FCSTD DOCUMENT  (FreeCAD 0.21R33771 (Git))
Label: enclousre
License: All rights reserved
LicenseURL: http://en.wikipedia.org/wiki/All_rights_reserved
objects: Part::Feature×48, App::Link×17, App::Part×7, Sketcher::SketchObject×3, PartDesign::Body×2, PartDesign::CoordinateSystem×1, Spreadsheet::Sheet×1, PartDesign::Pad×1
note: 56 computed .brp shape members not serialized (recipe doc carries the construction recipe); baked Part::Feature solids carry a one-line shape summary decoded from their .brp

FEATURE [PartDesign::CoordinateSystem] Local_CS_4743
  AttacherType = Attacher::AttachEngine3D
  MapMode = 2
  Support = -> [X_Axis001]
FEATURE [Part::Feature] Pcb_4743
  Placement = pos=(-69.596,105.156,0) rot=(0,0,1;0rad)
  shape: bbox 160.8 x 51.31 x 1.6 mm, 62 faces (baked)
FEATURE [Sketcher::SketchObject] PCB_Sketch_4743
  FullyConstrained = false
  sketch-geometry (4):
    g0: LineSegment StartX=0 StartY=51.308 StartZ=0 EndX=160.782 EndY=51.308 EndZ=0
    g1: LineSegment StartX=160.782 StartY=51.308 StartZ=0 EndX=160.782 EndY=0 EndZ=0
    g2: LineSegment StartX=160.782 StartY=0 StartZ=0 EndX=0 EndY=0 EndZ=0
    g3: LineSegment StartX=0 StartY=0 StartZ=0 EndX=0 EndY=51.308 EndZ=0
  constraints (4):
    c: Coincident(g2,g3)
    c: Coincident(g0,g3)
    c: Coincident(g1,g2)
    c: Coincident(g0,g1)
FEATURE [Part::Feature] Shape  label="R8_R_0805_2012Metric_542de8cd5894"
  Placement = pos=(126.088,23.921,0) rot=(0,0,1;3.14159rad)
  shape: bbox 2 x 1.2 x 0.45 mm, 26 faces (baked)
FEATURE [Part::Feature] Shape001  label="D4_LED_0805_2012Metric_c15a0e7d9ebd"
  Placement = pos=(60.614,23.921,0) rot=(0,0,1;0rad)
  shape: bbox 2 x 1.25 x 1.1 mm, 50 faces (baked)
FEATURE [App::Link] D4_LED_0805_2012Metric_c15a0e7d9ebd_ln_  label="D8_LED_0805_2012Metric_47b09096554b"
  LinkPlacement = pos=(121.678,23.921,0) rot=(0,0,1;0rad)
  LinkedObject = -> Shape001
  Placement = pos=(121.678,23.921,0) rot=(0,0,1;0rad)
FEATURE [Part::Feature] Arduino_Nano_WithMountingHoles
  shape: bbox 43.59 x 4.635 x 18 mm, 378 faces, 0 solids (baked)
FEATURE [Part::Feature] Arduino_Nano_WithMountingHoles001
  Placement = pos=(-1.143,1.6,-7.62) rot=(0,0,1;0rad)
  shape: bbox 5 x 11.75 x 2.54 mm, 46 faces, 0 solids (baked)
FEATURE [Part::Feature] Arduino_Nano_WithMountingHoles002
  Placement = pos=(-1.143,1.6,-5.08) rot=(0,0,1;0rad)
  shape: bbox 5 x 11.75 x 2.54 mm, 46 faces, 0 solids (baked)
FEATURE [Part::Feature] Arduino_Nano_WithMountingHoles003
  Placement = pos=(-1.143,1.6,-10.16) rot=(0,0,1;0rad)
  shape: bbox 5 x 11.75 x 2.54 mm, 46 faces, 0 solids (baked)
FEATURE [Part::Feature] Arduino_Nano_WithMountingHoles004
  Placement = pos=(0,0,0) rot=(0.707107,0,0.707107;3.14159rad)
  shape: bbox 38.1 x 11.75 x 2.54 mm, 364 faces, 0 solids (baked)
FEATURE [Part::Feature] Arduino_Nano_WithMountingHoles005
  Placement = pos=(0,0,-15.24) rot=(0.707107,0,0.707107;3.14159rad)
  shape: bbox 38.1 x 11.75 x 2.54 mm, 364 faces, 0 solids (baked)
FEATURE [Part::Feature] Arduino_Nano_WithMountingHoles006
  Placement = pos=(23.85,1.75,-7.62) rot=(0,1,0;3.92699rad)
  shape: bbox 11.38 x 1.1 x 11.38 mm, 1867 faces, 0 solids (baked)
FEATURE [Part::Feature] Arduino_Nano_WithMountingHoles007
  Placement = pos=(29.05,0,-7.67) rot=(0.707107,0,-0.707107;3.14159rad)
  shape: bbox 10.32 x 1.9 x 9.71 mm, 717 faces, 0 solids (baked)
FEATURE [Part::Feature] Arduino_Nano_WithMountingHoles008
  Placement = pos=(21.86,0,-5.8) rot=(0.707107,0,-0.707107;3.14159rad)
  shape: bbox 3.8 x 0.6 x 1.7 mm, 74 faces, 0 solids (baked)
FEATURE [Part::Feature] Arduino_Nano_WithMountingHoles009
  Placement = pos=(21.86,0,-9) rot=(0.707107,0,-0.707107;3.14159rad)
  shape: bbox 3.8 x 0.6 x 1.7 mm, 74 faces, 0 solids (baked)
FEATURE [Part::Feature] Arduino_Nano_WithMountingHoles010
  Placement = pos=(36.75,0,-7.6) rot=(0.707107,0,-0.707107;3.14159rad)
  shape: bbox 3.8 x 0.6 x 1.7 mm, 74 faces, 0 solids (baked)
FEATURE [Part::Feature] Arduino_Nano_WithMountingHoles011
  Placement = pos=(36.75,0,-12) rot=(0.707107,0,-0.707107;3.14159rad)
  shape: bbox 3.8 x 0.6 x 1.7 mm, 74 faces, 0 solids (baked)
FEATURE [Part::Feature] Arduino_Nano_WithMountingHoles012
  Placement = pos=(8.2,0,-2.6) rot=(0.707107,0,-0.707107;3.14159rad)
  shape: bbox 3.8 x 0.6 x 1.7 mm, 74 faces, 0 solids (baked)
FEATURE [Part::Feature] Arduino_Nano_WithMountingHoles013
  Placement = pos=(10.4,1.6,-2.8) rot=(0,0,1;0rad)
  shape: bbox 5.518 x 1.649 x 1.609 mm, 57 faces, 0 solids (baked)
FEATURE [Part::Feature] Arduino_Nano_WithMountingHoles014
  Placement = pos=(10.4,1.6,-5.55) rot=(0,0,1;0rad)
  shape: bbox 5.518 x 1.649 x 1.609 mm, 57 faces, 0 solids (baked)
FEATURE [Part::Feature] Arduino_Nano_WithMountingHoles015
  Placement = pos=(10.4,1.6,-12.5) rot=(0,0,1;0rad)
  shape: bbox 5.518 x 1.649 x 1.609 mm, 57 faces, 0 solids (baked)
FEATURE [Part::Feature] Arduino_Nano_WithMountingHoles016
  Placement = pos=(10.4,1.6,-9.05) rot=(0,0,1;0rad)
  shape: bbox 5.518 x 1.649 x 1.609 mm, 57 faces, 0 solids (baked)
FEATURE [Part::Feature] Arduino_Nano_WithMountingHoles017
  Placement = pos=(18.5113,1.6,-3.55414) rot=(0,-1,0;0.785398rad)
  shape: bbox 3.818 x 0.8 x 3.818 mm, 71 faces, 0 solids (baked)
FEATURE [Part::Feature] Arduino_Nano_WithMountingHoles018
  Placement = pos=(38.98,1.65,-7.62) rot=(0,-1,0;1.5708rad)
  shape: bbox 9.474 x 3.821 x 11.03 mm, 243 faces, 0 solids (baked)
FEATURE [Part::Feature] Arduino_Nano_WithMountingHoles019
  Placement = pos=(32.28,1.65,-7.62) rot=(0,1,0;1.5708rad)
  shape: bbox 8.2 x 4.5 x 7.7 mm, 127 faces, 0 solids (baked)
FEATURE [Part::Feature] Arduino_Nano_WithMountingHoles020 .. Arduino_Nano_WithMountingHoles024  x5 (patterned run collapsed; names and placements below)
  shape: bbox 9.422 x 2.565 x 0.5 mm, 31 faces, 0 solids (baked)
  placements: 5 in arithmetic series — first pos=(33.28,1.65,-9.22) rot=(0,1,0;1.5708rad), step (0,0,0.8), last pos=(33.28,1.65,-6.02) rot=(0,1,0;1.5708rad)
FEATURE [Part::Feature] Arduino_Nano_WithMountingHoles025
  Placement = pos=(37.2,0,-3.3) rot=(0.707107,0,0.707107;3.14159rad)
  shape: bbox 4 x 1.81 x 1.7 mm, 124 faces, 0 solids (baked)
FEATURE [Part::Feature] Arduino_Nano_WithMountingHoles026
  Placement = pos=(7.9,0,-5.6) rot=(0.707107,0,-0.707107;3.14159rad)
  shape: bbox 4 x 1.81 x 1.7 mm, 124 faces, 0 solids (baked)
FEATURE [Part::Feature] Arduino_Nano_WithMountingHoles027
  Placement = pos=(15.25,1.6,-8.05) rot=(0,1,0;1.5708rad)
  shape: bbox 2.8 x 2.156 x 5.2 mm, 77 faces, 0 solids (baked)
FEATURE [Part::Feature] Arduino_Nano_WithMountingHoles028
  Placement = pos=(15.25,3.25,-8.05) rot=(0,0,1;0rad)
  shape: bbox 3.003 x 1.653 x 4.003 mm, 100 faces, 0 solids (baked)
FEATURE [Part::Feature] Arduino_Nano_WithMountingHoles029
  Placement = pos=(6.1,0,-10.16) rot=(0.707107,0,-0.707107;3.14159rad)
  shape: bbox 8.3 x 1.69 x 6.5 mm, 198 faces, 0 solids (baked)
FEATURE [Part::Feature] Arduino_Nano_WithMountingHoles030
  Placement = pos=(11.43,0,-4.2) rot=(0.707107,0,0.707107;3.14159rad)
  shape: bbox 1.7 x 1.384 x 4.916 mm, 85 faces, 0 solids (baked)
FEATURE [Part::Feature] Arduino_Nano_WithMountingHoles031
  Placement = pos=(15.75,0,-10.85) rot=(0.707107,0,0.707107;3.14159rad)
  shape: bbox 3 x 0.5241 x 3.2 mm, 288 faces, 0 solids (baked)
FEATURE [Part::Feature] Arduino_Nano_WithMountingHoles032
  Placement = pos=(15.75,0,-5.2) rot=(0.707107,0,0.707107;3.14159rad)
  shape: bbox 3 x 0.5241 x 3.2 mm, 277 faces, 0 solids (baked)
FEATURE [App::Part] Arduino_Nano_WithMountingHoles033  label="A1_Arduino_Nano_WithMountingHoles033_add46494fcf4"
  Group = -> [Arduino_Nano_WithMountingHoles,Arduino_Nano_WithMountingHoles001,Arduino_Nano_WithMountingHoles002,Arduino_Nano_WithMountingHoles003,Arduino_Nano_WithMountingHoles004,Arduino_Nano_WithMountingHoles005,Arduino_Nano_WithMountingHoles006,Arduino_Nano_WithMountingHoles007,Arduino_Nano_WithMountingHoles008,Arduino_Nano_WithMountingHoles009,Arduino_Nano_WithMountingHoles010,+22 more]
  Origin = -> Origin008
  Placement = pos=(148.59,8.9,3.1) rot=(-0.57735,-0.57735,-0.57735;4.18879rad)
FEATURE [Part::Feature] Part__Feature  label="Neutrik NC3FAH2"
  shape: bbox 1.44 x 13.29 x 15.76 mm, 58 faces (baked)
FEATURE [Part::Feature] Part__Feature001  label="Neutrik NC3FAH003"
  shape: bbox 10.2 x 7.623 x 28.18 mm, 194 faces (baked)
FEATURE [Part::Feature] Part__Feature002  label="Neutrik NC3FAH004"
  shape: bbox 6 x 16.35 x 8 mm, 28 faces (baked)
FEATURE [Part::Feature] Part__Feature003  label="Neutrik NC3FAH005"
  shape: bbox 6 x 16.35 x 8 mm, 28 faces (baked)
FEATURE [Part::Feature] Part__Feature004  label="Neutrik NC3FAH006"
  shape: bbox 6 x 12.35 x 8 mm, 24 faces (baked)
FEATURE [Part::Feature] Part__Feature005  label="Neutrik NC3FAH007"
  shape: bbox 27.2 x 27.96 x 22.65 mm, 962 faces (baked)
FEATURE [App::Part] Neutrik_NC3FAH008  label="J3_Neutrik NC3FAH008_ddd3292a21dc"
  Group = -> [Part__Feature,Part__Feature001,Part__Feature002,Part__Feature003,Part__Feature004,Part__Feature005]
  Origin = -> Origin009
  Placement = pos=(84.16,48.31,0) rot=(1,0,0;1.5708rad)
FEATURE [App::Link] D4_LED_0805_2012Metric_c15a0e7d9ebd_ln_001  label="D6_LED_0805_2012Metric_a3d814ee4790"
  LinkPlacement = pos=(72.6555,23.921,0) rot=(0,0,1;0rad)
  LinkedObject = -> Shape001
  Placement = pos=(72.6555,23.921,0) rot=(0,0,1;0rad)
FEATURE [App::Link] R8_R_0805_2012Metric_542de8cd5894_ln_  label="R4_R_0805_2012Metric_9a44cdb4aa3b"
  LinkPlacement = pos=(46.0775,23.921,0) rot=(0,0,1;0rad)
  LinkedObject = -> Shape
  Placement = pos=(46.0775,23.921,0) rot=(0,0,1;0rad)
FEATURE [App::Link] R8_R_0805_2012Metric_542de8cd5894_ln_001  label="R5_R_0805_2012Metric_4d9526face75"
  LinkPlacement = pos=(77.216,23.921,0) rot=(0,0,1;0rad)
  LinkedObject = -> Shape
  Placement = pos=(77.216,23.921,0) rot=(0,0,1;0rad)
FEATURE [App::Link] D4_LED_0805_2012Metric_c15a0e7d9ebd_ln_002  label="D2_LED_0805_2012Metric_bbd0da5a3e7d"
  LinkPlacement = pos=(41.8315,23.921,0) rot=(0,0,1;0rad)
  LinkedObject = -> Shape001
  Placement = pos=(41.8315,23.921,0) rot=(0,0,1;0rad)
FEATURE [App::Link] R8_R_0805_2012Metric_542de8cd5894_ln_002  label="R2_R_0805_2012Metric_ba1683f544c3"
  LinkPlacement = pos=(34.1865,23.921,0) rot=(0,0,1;3.14159rad)
  LinkedObject = -> Shape
  Placement = pos=(34.1865,23.921,0) rot=(0,0,1;3.14159rad)
FEATURE [App::Link] R8_R_0805_2012Metric_542de8cd5894_ln_003  label="R6_R_0805_2012Metric_406797a00f78"
  LinkPlacement = pos=(107.546,23.921,0) rot=(0,0,1;0rad)
  LinkedObject = -> Shape
  Placement = pos=(107.546,23.921,0) rot=(0,0,1;0rad)
FEATURE [App::Link] J3_Neutrik_NC3FAH008_ddd3292a21dc_ln_  label="J1_Neutrik NC3FAH008_6e6a4ee42cfc"
  LinkPlacement = pos=(23.204,48.306,0) rot=(1,0,0;1.5708rad)
  LinkedObject = -> Neutrik_NC3FAH008
  Placement = pos=(23.204,48.306,0) rot=(1,0,0;1.5708rad)
FEATURE [App::Link] D4_LED_0805_2012Metric_c15a0e7d9ebd_ln_003  label="D3_LED_0805_2012Metric_1a4d4566548c"
  LinkPlacement = pos=(29.7765,23.921,0) rot=(0,0,1;0rad)
  LinkedObject = -> Shape001
  Placement = pos=(29.7765,23.921,0) rot=(0,0,1;0rad)
FEATURE [App::Link] D4_LED_0805_2012Metric_c15a0e7d9ebd_ln_004  label="D1_LED_0805_2012Metric_465b72bef6d4"
  LinkPlacement = pos=(12.0165,23.921,0) rot=(0,0,1;0rad)
  LinkedObject = -> Shape001
  Placement = pos=(12.0165,23.921,0) rot=(0,0,1;0rad)
FEATURE [App::Link] R8_R_0805_2012Metric_542de8cd5894_ln_004  label="R7_R_0805_2012Metric_9987731a8ca5"
  LinkPlacement = pos=(95.5175,23.921,0) rot=(0,0,1;3.14159rad)
  LinkedObject = -> Shape
  Placement = pos=(95.5175,23.921,0) rot=(0,0,1;3.14159rad)
FEATURE [App::Link] J3_Neutrik_NC3FAH008_ddd3292a21dc_ln_001  label="J4_Neutrik NC3FAH008_f1a8b087ef94"
  LinkPlacement = pos=(114.644,48.306,0) rot=(1,0,0;1.5708rad)
  LinkedObject = -> Neutrik_NC3FAH008
  Placement = pos=(114.644,48.306,0) rot=(1,0,0;1.5708rad)
FEATURE [App::Link] R8_R_0805_2012Metric_542de8cd5894_ln_005  label="R1_R_0805_2012Metric_d44ece5b64db"
  LinkPlacement = pos=(16.4265,23.921,0) rot=(0,0,1;0rad)
  LinkedObject = -> Shape
  Placement = pos=(16.4265,23.921,0) rot=(0,0,1;0rad)
FEATURE [App::Link] D4_LED_0805_2012Metric_c15a0e7d9ebd_ln_005  label="D7_LED_0805_2012Metric_17e1e7723463"
  LinkPlacement = pos=(103.202,23.921,0) rot=(0,0,1;0rad)
  LinkedObject = -> Shape001
  Placement = pos=(103.202,23.921,0) rot=(0,0,1;0rad)
FEATURE [App::Link] R8_R_0805_2012Metric_542de8cd5894_ln_006  label="R3_R_0805_2012Metric_9e949f457a33"
  LinkPlacement = pos=(65.024,23.921,0) rot=(0,0,1;3.14159rad)
  LinkedObject = -> Shape
  Placement = pos=(65.024,23.921,0) rot=(0,0,1;3.14159rad)
FEATURE [App::Link] J3_Neutrik_NC3FAH008_ddd3292a21dc_ln_002  label="J2_Neutrik NC3FAH008_c8d545dbce63"
  LinkPlacement = pos=(53.684,48.306,0) rot=(1,0,0;1.5708rad)
  LinkedObject = -> Neutrik_NC3FAH008
  Placement = pos=(53.684,48.306,0) rot=(1,0,0;1.5708rad)
FEATURE [App::Link] D4_LED_0805_2012Metric_c15a0e7d9ebd_ln_006  label="D5_LED_0805_2012Metric_2f24e8875b89"
  LinkPlacement = pos=(91.1075,23.921,0) rot=(0,0,1;0rad)
  LinkedObject = -> Shape001
  Placement = pos=(91.1075,23.921,0) rot=(0,0,1;0rad)
FEATURE [App::Part] Top_4743
  Group = -> [Shape,Shape001,D4_LED_0805_2012Metric_c15a0e7d9ebd_ln_,Arduino_Nano_WithMountingHoles033,Neutrik_NC3FAH008,D4_LED_0805_2012Metric_c15a0e7d9ebd_ln_001,R8_R_0805_2012Metric_542de8cd5894_ln_,R8_R_0805_2012Metric_542de8cd5894_ln_001,D4_LED_0805_2012Metric_c15a0e7d9ebd_ln_002,R8_R_0805_2012Metric_542de8cd5894_ln_002,R8_R_0805_2012Metric_542de8cd5894_ln_003,J3_Neutrik_NC3FAH008_ddd3292a21dc_ln_,+9 more]
  Origin = -> Origin003
FEATURE [App::Part] Step_Models_4743
  Group = -> [Top_4743]
  Origin = -> Origin002
FEATURE [Part::Feature] pads_area001  label="topPads_4743"
  Placement = pos=(-69.596,105.156,0.02) rot=(0,0,1;0rad)
  shape: bbox 138.8 x 37.16 x 2e-07 mm, 82 faces, 0 solids (baked)
FEATURE [Part::Feature] Shape003  label="topTracks_4743"
  Placement = pos=(-69.596,105.156,0.01) rot=(0,0,1;0rad)
  shape: bbox 137.4 x 34.4 x 2e-07 mm, 33 faces, 0 solids (baked)
FEATURE [Part::Feature] zones_area001  label="topZones_4743"
  Placement = pos=(-69.596,105.156,0.01) rot=(0,0,1;0rad)
  shape: bbox 160.8 x 51.36 x 2e-07 mm, 1 faces, 0 solids (baked)
FEATURE [Part::Feature] pads_area003  label="botPads_4743"
  Placement = pos=(-69.596,105.156,-1.62) rot=(0,0,1;0rad)
  shape: bbox 131.8 x 37.16 x 2e-07 mm, 50 faces, 0 solids (baked)
FEATURE [Part::Feature] Shape005  label="botTracks_4743"
  Placement = pos=(-69.596,105.156,-1.61) rot=(0,0,1;0rad)
  shape: bbox 124.9 x 25.05 x 2e-07 mm, 9 faces, 0 solids (baked)
FEATURE [Part::Feature] zones_area003  label="botZones_4743"
  Placement = pos=(-69.596,105.156,-1.61) rot=(0,0,1;0rad)
  shape: bbox 160.8 x 51.36 x 2e-07 mm, 1 faces, 0 solids (baked)
FEATURE [App::Part] Board_Geoms_4743
  Group = -> [Pcb_4743,PCB_Sketch_4743,pads_area001,Shape003,zones_area001,pads_area003,Shape005,zones_area003]
  Origin = -> Origin
FEATURE [App::Part] Board_4743  label="PCB"
  Group = -> [Local_CS_4743,Board_Geoms_4743,Step_Models_4743]
  Origin = -> Origin001
  Placement = pos=(4,6,8) rot=(0,0,1;0rad)
  expr: .Placement.Base.x = Spreadsheet.wall_thickness + Spreadsheet.pcb_clearance
  expr: .Placement.Base.y = Spreadsheet.wall_thickness + Spreadsheet.pcb_clearance * 2
  expr: .Placement.Base.z = Spreadsheet.wall_thickness + Spreadsheet.pcb_Standoff
FEATURE [Spreadsheet::Sheet] Spreadsheet
  cells = A1='pcb_width; B1(pcb_width)=51.308; C1='mm; A2='pcb_length; B2(pcb_length)=160.782; C2='mm; A3='pcb_thickness; B3(pcb_thickness)=1.7; C3='mm; D3='estimate; A4='pcb_clearance; B4(pcb_clearance)=2; C4='mm; A5='wall_thickness; B5(wall_thickness)=2; C5='mm; A6='pcb_standoff; B6(pcb_Standoff)=6; C6='mm; A8='usb_height; B8(usb_height)=2.5; C8='mm; A9='usb_width; B9(usb_width)=7.8; C9='mm; A10='usb_depth; B10(usb_depth)=4; C10='mm; A11='usb_extend_in; B11(usb_extend_in)=2; C11='mm; A12='usb_extend_out; B12(usb_extend_out)=2; C12='mm; A13='usb_clearance; B13(usb_clearance)=2; C13='mm; A14='xlr_depth; B14(xlr_depth)=; A15='xlr_radius; B15(xlr_radius)=
FEATURE [Sketcher::SketchObject] Sketch
  FullyConstrained = true
  MapMode = 5
  Support = -> [XY_Plane011]
  expr: Constraints[8] = Spreadsheet.wall_thickness * 2 + Spreadsheet.pcb_clearance * 2 + Spreadsheet.pcb_length
  expr: Constraints[9] = Spreadsheet.wall_thickness * 2 + Spreadsheet.pcb_clearance * 2 + Spreadsheet.pcb_width
  sketch-geometry (4):
    g0: LineSegment StartX=0 StartY=59.308 StartZ=0 EndX=168.782 EndY=59.308 EndZ=0
    g1: LineSegment StartX=168.782 StartY=59.308 StartZ=0 EndX=168.782 EndY=0 EndZ=0
    g2: LineSegment StartX=168.782 StartY=0 StartZ=0 EndX=0 EndY=0 EndZ=0
    g3: LineSegment StartX=0 StartY=0 StartZ=0 EndX=0 EndY=59.308 EndZ=0
  constraints (11):
    c: Coincident(g0,g1)
    c: Coincident(g1,g2)
    c: Coincident(g2,g3)
    c: Coincident(g3,g0)
    c: Horizontal(g0)
    c: Horizontal(g2)
    c: Vertical(g1)
    c: Vertical(g3)
    c: DistanceX(g0,g0) = 168.782
    c: DistanceY(g1,g1) = 59.308
    c: Coincident(g2,g-1)
FEATURE [PartDesign::Pad] Pad
  Direction = (0,0,1)
  Length = 40
  Length2 = 10
  Profile = -> Sketch
  ReferenceAxis = -> Sketch [N_Axis]
  Type = 0
FEATURE [PartDesign::Body] Body  label="exterior case"
  Group = -> [Sketch,Pad]
  Origin = -> Origin011
  Tip = -> Pad
FEATURE [Sketcher::SketchObject] Sketch001
  FullyConstrained = false
  MapMode = 5
  Support = -> [XY_Plane012]
  expr: Constraints[8] = Spreadsheet.usb_width
  expr: Constraints[9] = Spreadsheet.usb_depth + Spreadsheet.usb_extend_in + Spreadsheet.usb_extend_out
  sketch-geometry (4):
    g0: LineSegment StartX=141.084 StartY=58.1464 StartZ=0 EndX=148.884 EndY=58.1464 EndZ=0
    g1: LineSegment StartX=148.884 StartY=58.1464 StartZ=0 EndX=148.884 EndY=50.1464 EndZ=0
    g2: LineSegment StartX=148.884 StartY=50.1464 StartZ=0 EndX=141.084 EndY=50.1464 EndZ=0
    g3: LineSegment StartX=141.084 StartY=50.1464 StartZ=0 EndX=141.084 EndY=58.1464 EndZ=0
  constraints (10):
    c: Coincident(g0,g1)
    c: Coincident(g1,g2)
    c: Coincident(g2,g3)
    c: Coincident(g3,g0)
    c: Horizontal(g0)
    c: Horizontal(g2)
    c: Vertical(g1)
    c: Vertical(g3)
    c: DistanceX(g0,g0) = 7.8
    c: DistanceY(g1,g1) = 8
FEATURE [PartDesign::Body] Body001  label="usb port hole"
  Group = -> [Sketch001]
  Origin = -> Origin012
FEATURE [App::Part] Part  label="Case"
  Group = -> [Body,Body001]
  Origin = -> Origin010
